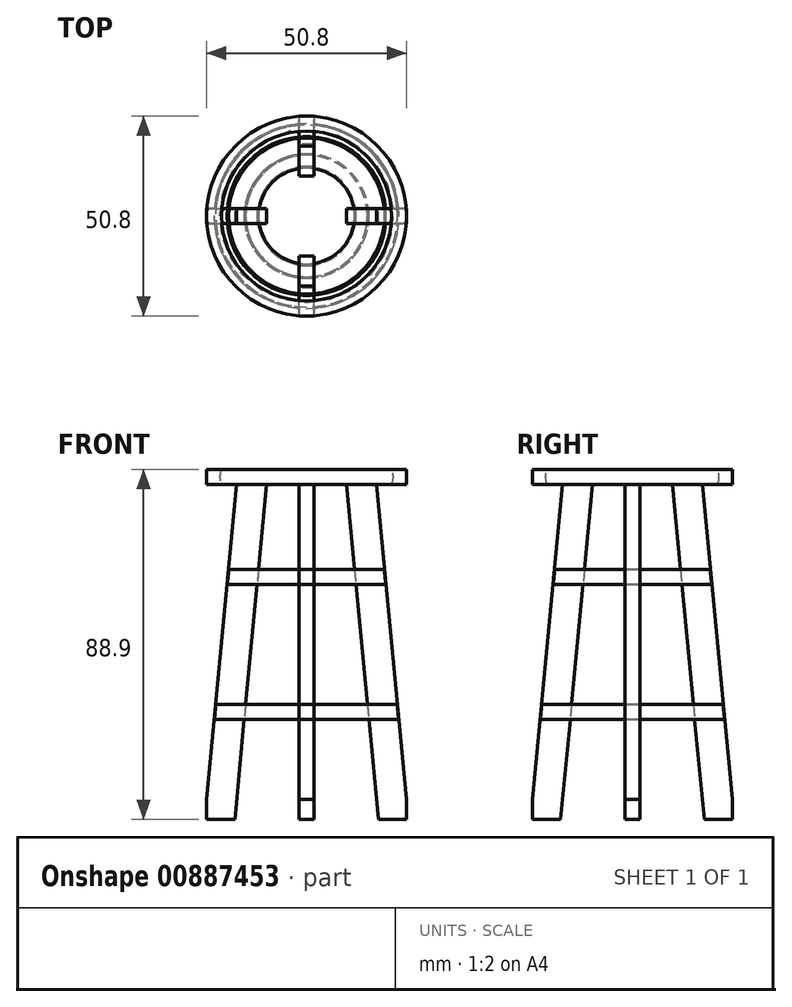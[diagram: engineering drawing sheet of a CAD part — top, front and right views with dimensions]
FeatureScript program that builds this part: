
annotation { "Feature Type Name" : "Feature", "Feature Type Description" : "" }
export const myFeature = defineFeature(function(context is Context, id is Id, definition is map)
    precondition{}
    {
        {
            var Q0;
            Q0=qCreatedBy(makeId("Front.planeOp"),FACE);
            var sketch = newSketch(context, id + "F0", { "sketchPlane" : qUnion([Q0])});
            skLineSegment(sketch, "E0.bottom", {"start": v(25.4, 44.45) * mm, "end": v(-25.4, 44.45) * mm});
            skLineSegment(sketch, "E0.top", {"start": v(25.4, -44.45) * mm, "end": v(-25.4, -44.45) * mm});
            skLineSegment(sketch, "E0.left", {"start": v(25.4, 44.45) * mm, "end": v(25.4, -44.45) * mm});
            skLineSegment(sketch, "E0.right", {"start": v(-25.4, 44.45) * mm, "end": v(-25.4, -44.45) * mm});
            skPoint(sketch, "E0.middle", {"position": v(0, 0) * mm});
            skLineSegment(sketch, "E1", {"start": v(-25.4, 40.64) * mm, "end": v(25.4, 40.64) * mm});
            skArc(sketch, "E2", {"start": v(-21.59, 40.64) * mm, "mid": v(-22.04, 42.55) * mm, "end": v(-21.59, 44.45) * mm});
            skArc(sketch, "E3", {"start": v(21.59, 44.45) * mm, "mid": v(22.04, 42.55) * mm, "end": v(21.6, 40.64) * mm});
            skPoint(sketch, "E4.end.orphan", {"position": v(21.59, 40.64) * mm});
            skPoint(sketch, "E5.start.orphan", {"position": v(21.59, 42.55) * mm});
            skPoint(sketch, "E6.start.orphan", {"position": v(-21.59, 44.45) * mm});
            skPoint(sketch, "E7.start.orphan", {"position": v(-21.59, 42.55) * mm});
            skLineSegment(sketch, "E8", {"start": v(-17.75, -39.37) * mm, "end": v(17.75, -39.37) * mm});
            skLineSegment(sketch, "E9", {"start": v(-25.4, -39.37) * mm, "end": v(-17.78, 40.64) * mm});
            skLineSegment(sketch, "E10", {"start": v(17.78, 40.64) * mm, "end": v(25.4, -39.37) * mm});
            skLineSegment(sketch, "E11", {"start": v(-18.23, -44.45) * mm, "end": v(-10.13, 40.64) * mm});
            skLineSegment(sketch, "E12", {"start": v(10.13, 40.64) * mm, "end": v(18.23, -44.45) * mm});
            skPoint(sketch, "E13.end.orphan", {"position": v(17.78, 0) * mm});
            skPoint(sketch, "E14.orphan", {"position": v(-25.4, 0) * mm});
            skPoint(sketch, "E15.orphan", {"position": v(25.4, 0) * mm});
            skLineSegment(sketch, "E16", {"start": v(-20.2, 15.24) * mm, "end": v(20.2, 15.24) * mm});
            skLineSegment(sketch, "E17", {"start": v(-23.46, -19.05) * mm, "end": v(23.46, -19.05) * mm});
            skLineSegment(sketch, "E18.0", {"start": v(-23.1, -15.24) * mm, "end": v(23.1, -15.24) * mm});
            skLineSegment(sketch, "E19.0", {"start": v(-19.84, 19.05) * mm, "end": v(19.84, 19.05) * mm});
            skLineSegment(sketch, "E20", {"start": v(0, 40.64) * mm, "end": v(0, 44.45) * mm});
            skLineSegment(sketch, "E21", {"start": v(0, 44.45) * mm, "end": v(0, 48.34) * mm});
            skLineSegment(sketch, "E22", {"start": v(0, 40.64) * mm, "end": v(0, 36.32) * mm});
            skLineSegment(sketch, "E23", {"start": v(0, 36.32) * mm, "end": v(0, 48.34) * mm});
            skPoint(sketch, "E24.endSnap0", {"position": v(0, 15.24) * mm});
            skPoint(sketch, "E24.end.orphan", {"position": v(0, 21.51) * mm});
            skLineSegment(sketch, "E25", {"start": v(0, 36.32) * mm, "end": v(0, -26.6) * mm});
            skSolve(sketch);
        }
        {
            var Q0;
            {var subQ5=sQuery(id+"F0.wireOp",EDGE,"E2");Q0=makeQuery(id+"F0.imprint","IMPRINT",FACE,{"disambiguationData":[TD([[makeQuery(id+"F0.imprint","IMPRINT",EDGE,{"derivedFrom":subQ5}),-1.0]])]});}
            var Q1;
            Q1=sQuery(id+"F0.wireOp",EDGE,"E20");
            revolve(context, id + "F1", {"surfaceOperationType" : NewSurfaceOperationType.NEW, "entities" : qUnion([Q0]), "axis" : qUnion([Q1]), "revolveType" : RevolveType.FULL});
        }
        {
            var Q0;
            {var subQ0=sQuery(id+"F0.wireOp",EDGE,"E9");var subQ1=sQuery(id+"F0.wireOp",EDGE,"E1");var subQ2=makeQuery(id+"F0.imprint","INTERSECT",VERTEX,{"derivedFrom":[subQ1,subQ0]});Q0=makeQuery(id+"F0.imprint","IMPRINT",FACE,{"disambiguationData":[TD([[makeQuery(id+"F0.imprint","IMPRINT",EDGE,{"disambiguationData":[TD([[subQ2,-1.0]])],"derivedFrom":subQ1}),-1.0]])]});}
            var Q1;
            {var subQ0=sQuery(id+"F0.wireOp",EDGE,"E16");var subQ1=sQuery(id+"F0.wireOp",EDGE,"E9");var subQ2=makeQuery(id+"F0.imprint","INTERSECT",VERTEX,{"derivedFrom":[subQ1,subQ0]});Q1=makeQuery(id+"F0.imprint","IMPRINT",FACE,{"disambiguationData":[TD([[makeQuery(id+"F0.imprint","IMPRINT",EDGE,{"disambiguationData":[TD([[subQ2,-1.0]])],"derivedFrom":subQ1}),-1.0]])]});}
            var Q2;
            {var subQ0=sQuery(id+"F0.wireOp",EDGE,"E16");var subQ1=sQuery(id+"F0.wireOp",EDGE,"E9");var subQ2=makeQuery(id+"F0.imprint","INTERSECT",VERTEX,{"derivedFrom":[subQ1,subQ0]});Q2=makeQuery(id+"F0.imprint","IMPRINT",FACE,{"disambiguationData":[TD([[makeQuery(id+"F0.imprint","IMPRINT",EDGE,{"disambiguationData":[TD([[subQ2,1.0]])],"derivedFrom":subQ1}),-1.0]])]});}
            var Q3;
            {var subQ0=sQuery(id+"F0.wireOp",EDGE,"E17");var subQ1=sQuery(id+"F0.wireOp",EDGE,"E9");var subQ2=makeQuery(id+"F0.imprint","INTERSECT",VERTEX,{"derivedFrom":[subQ1,subQ0]});Q3=makeQuery(id+"F0.imprint","IMPRINT",FACE,{"disambiguationData":[TD([[makeQuery(id+"F0.imprint","IMPRINT",EDGE,{"disambiguationData":[TD([[subQ2,-1.0]])],"derivedFrom":subQ1}),-1.0]])]});}
            var Q4;
            {var subQ2=sQuery(id+"F0.wireOp",EDGE,"E0.top");var subQ4=sQuery(id+"F0.wireOp",EDGE,"E0.right");var subQ5=makeQuery(id+"F0.imprint","INTERSECT",VERTEX,{"derivedFrom":[subQ2,subQ4]});Q4=makeQuery(id+"F0.imprint","IMPRINT",FACE,{"disambiguationData":[TD([[makeQuery(id+"F0.imprint","IMPRINT",EDGE,{"disambiguationData":[TD([[subQ5,1.0]])],"derivedFrom":subQ2}),-1.0]])]});}
            var Q5;
            {var subQ0=sQuery(id+"F0.wireOp",EDGE,"E17");var subQ1=sQuery(id+"F0.wireOp",EDGE,"E10");var subQ2=makeQuery(id+"F0.imprint","INTERSECT",VERTEX,{"derivedFrom":[subQ1,subQ0]});Q5=makeQuery(id+"F0.imprint","IMPRINT",FACE,{"disambiguationData":[TD([[makeQuery(id+"F0.imprint","IMPRINT",EDGE,{"disambiguationData":[TD([[subQ2,1.0]])],"derivedFrom":subQ1}),-1.0]])]});}
            var Q6;
            {var subQ1=sQuery(id+"F0.wireOp",EDGE,"E0.left");var subQ8=sQuery(id+"F0.wireOp",EDGE,"E0.top");var subQ9=makeQuery(id+"F0.imprint","INTERSECT",VERTEX,{"derivedFrom":[subQ8,subQ1]});Q6=makeQuery(id+"F0.imprint","IMPRINT",FACE,{"disambiguationData":[TD([[makeQuery(id+"F0.imprint","IMPRINT",EDGE,{"disambiguationData":[TD([[subQ9,-1.0]])],"derivedFrom":subQ8}),-1.0]])]});}
            var Q7;
            {var subQ0=sQuery(id+"F0.wireOp",EDGE,"E16");var subQ1=sQuery(id+"F0.wireOp",EDGE,"E10");var subQ2=makeQuery(id+"F0.imprint","INTERSECT",VERTEX,{"derivedFrom":[subQ1,subQ0]});Q7=makeQuery(id+"F0.imprint","IMPRINT",FACE,{"disambiguationData":[TD([[makeQuery(id+"F0.imprint","IMPRINT",EDGE,{"disambiguationData":[TD([[subQ2,-1.0]])],"derivedFrom":subQ1}),-1.0]])]});}
            var Q8;
            {var subQ0=sQuery(id+"F0.wireOp",EDGE,"E16");var subQ1=sQuery(id+"F0.wireOp",EDGE,"E10");var subQ2=makeQuery(id+"F0.imprint","INTERSECT",VERTEX,{"derivedFrom":[subQ1,subQ0]});Q8=makeQuery(id+"F0.imprint","IMPRINT",FACE,{"disambiguationData":[TD([[makeQuery(id+"F0.imprint","IMPRINT",EDGE,{"disambiguationData":[TD([[subQ2,1.0]])],"derivedFrom":subQ1}),-1.0]])]});}
            var Q9;
            {var subQ0=sQuery(id+"F0.wireOp",EDGE,"E10");var subQ1=sQuery(id+"F0.wireOp",EDGE,"E1");var subQ2=makeQuery(id+"F0.imprint","INTERSECT",VERTEX,{"derivedFrom":[subQ1,subQ0]});Q9=makeQuery(id+"F0.imprint","IMPRINT",FACE,{"disambiguationData":[TD([[makeQuery(id+"F0.imprint","IMPRINT",EDGE,{"disambiguationData":[TD([[subQ2,1.0]])],"derivedFrom":subQ1}),-1.0]])]});}
            extrude(context, id + "F2", {"entities" : qUnion([Q0, Q1, Q2, Q3, Q4, Q5, Q6, Q7, Q8, Q9]), "operationType" : NewBodyOperationType.ADD, "endBound" : BoundingType.SYMMETRIC, "depth" : 3.8 * mm, "offsetDistance" : 25.4 * mm});
        }
        {
            var Q0;
            Q0=qCreatedBy(makeId("Right.planeOp"),FACE);
            var sketch = newSketch(context, id + "F3", { "sketchPlane" : qUnion([Q0])});
            skLineSegment(sketch, "E26.bottom", {"start": v(25.4, 44.45) * mm, "end": v(-25.4, 44.45) * mm});
            skLineSegment(sketch, "E26.top", {"start": v(25.4, -44.45) * mm, "end": v(-25.4, -44.45) * mm});
            skLineSegment(sketch, "E26.left", {"start": v(25.4, 44.45) * mm, "end": v(25.4, -44.45) * mm});
            skLineSegment(sketch, "E26.right", {"start": v(-25.4, 44.45) * mm, "end": v(-25.4, -44.45) * mm});
            skPoint(sketch, "E26.middle", {"position": v(0, 0) * mm});
            skLineSegment(sketch, "E27", {"start": v(-25.4, 40.64) * mm, "end": v(25.4, 40.64) * mm});
            skArc(sketch, "E28", {"start": v(-25.1, 40.64) * mm, "mid": v(-25.56, 42.54) * mm, "end": v(-25.1, 44.45) * mm});
            skArc(sketch, "E29", {"start": v(21.6, 44.45) * mm, "mid": v(23.22, 42.54) * mm, "end": v(21.6, 40.64) * mm});
            skPoint(sketch, "E30.end.orphan", {"position": v(21.6, 40.64) * mm});
            skPoint(sketch, "E31.start.orphan", {"position": v(21.6, 42.54) * mm});
            skPoint(sketch, "E32.start.orphan", {"position": v(-25.1, 44.45) * mm});
            skPoint(sketch, "E33.start.orphan", {"position": v(-25.1, 42.54) * mm});
            skLineSegment(sketch, "E34", {"start": v(-17.75, -39.37) * mm, "end": v(17.75, -39.37) * mm});
            skLineSegment(sketch, "E35", {"start": v(-25.4, -39.37) * mm, "end": v(-17.78, 40.64) * mm});
            skLineSegment(sketch, "E36", {"start": v(17.78, 40.64) * mm, "end": v(25.4, -39.37) * mm});
            skLineSegment(sketch, "E37", {"start": v(-18.23, -44.45) * mm, "end": v(-10.13, 40.64) * mm});
            skLineSegment(sketch, "E38", {"start": v(10.13, 40.64) * mm, "end": v(18.23, -44.45) * mm});
            skPoint(sketch, "E39.end.orphan", {"position": v(17.78, 0) * mm});
            skPoint(sketch, "E40.orphan", {"position": v(-25.4, 0) * mm});
            skPoint(sketch, "E41.orphan", {"position": v(25.4, 0) * mm});
            skLineSegment(sketch, "E42", {"start": v(-20.2, 15.24) * mm, "end": v(20.2, 15.24) * mm});
            skLineSegment(sketch, "E43", {"start": v(-23.46, -19.05) * mm, "end": v(23.46, -19.05) * mm});
            skLineSegment(sketch, "E44.0", {"start": v(-23.1, -15.24) * mm, "end": v(23.1, -15.24) * mm});
            skLineSegment(sketch, "E45.0", {"start": v(-19.84, 19.05) * mm, "end": v(19.84, 19.05) * mm});
            skLineSegment(sketch, "E46", {"start": v(0, 40.64) * mm, "end": v(0, 44.45) * mm});
            skLineSegment(sketch, "E47", {"start": v(0, 44.45) * mm, "end": v(0, 47.53) * mm});
            skLineSegment(sketch, "E48", {"start": v(0, 40.64) * mm, "end": v(0, 35.5) * mm});
            skLineSegment(sketch, "E49", {"start": v(0, 35.5) * mm, "end": v(0, 47.53) * mm});
            skPoint(sketch, "E50.endSnap0", {"position": v(0, 15.24) * mm});
            skPoint(sketch, "E50.end.orphan", {"position": v(0, 21.51) * mm});
            skLineSegment(sketch, "E51", {"start": v(0, 35.5) * mm, "end": v(0, -27.43) * mm});
            skLineSegment(sketch, "E52", {"start": v(21.6, 44.45) * mm, "end": v(21.6, 40.64) * mm});
            skLineSegment(sketch, "E53", {"start": v(17.78, 40.64) * mm, "end": v(17.78, 44.45) * mm});
            skSolve(sketch);
        }
        {
            var Q0;
            {var subQ0=sQuery(id+"F3.wireOp",EDGE,"E35");var subQ1=sQuery(id+"F3.wireOp",EDGE,"E27");var subQ2=makeQuery(id+"F3.imprint","INTERSECT",VERTEX,{"derivedFrom":[subQ1,subQ0]});Q0=makeQuery(id+"F3.imprint","IMPRINT",FACE,{"disambiguationData":[TD([[makeQuery(id+"F3.imprint","IMPRINT",EDGE,{"disambiguationData":[TD([[subQ2,-1.0]])],"derivedFrom":subQ1}),-1.0]])]});}
            var Q1;
            {var subQ0=sQuery(id+"F3.wireOp",EDGE,"E42");var subQ1=sQuery(id+"F3.wireOp",EDGE,"E35");var subQ2=makeQuery(id+"F3.imprint","INTERSECT",VERTEX,{"derivedFrom":[subQ1,subQ0]});Q1=makeQuery(id+"F3.imprint","IMPRINT",FACE,{"disambiguationData":[TD([[makeQuery(id+"F3.imprint","IMPRINT",EDGE,{"disambiguationData":[TD([[subQ2,-1.0]])],"derivedFrom":subQ1}),-1.0]])]});}
            var Q2;
            {var subQ0=sQuery(id+"F3.wireOp",EDGE,"E36");var subQ1=sQuery(id+"F3.wireOp",EDGE,"E27");var subQ2=makeQuery(id+"F3.imprint","INTERSECT",VERTEX,{"derivedFrom":[subQ1,subQ0]});Q2=makeQuery(id+"F3.imprint","IMPRINT",FACE,{"disambiguationData":[TD([[makeQuery(id+"F3.imprint","IMPRINT",EDGE,{"disambiguationData":[TD([[subQ2,1.0]])],"derivedFrom":subQ1}),-1.0]])]});}
            var Q3;
            {var subQ0=sQuery(id+"F3.wireOp",EDGE,"E42");var subQ1=sQuery(id+"F3.wireOp",EDGE,"E36");var subQ2=makeQuery(id+"F3.imprint","INTERSECT",VERTEX,{"derivedFrom":[subQ1,subQ0]});Q3=makeQuery(id+"F3.imprint","IMPRINT",FACE,{"disambiguationData":[TD([[makeQuery(id+"F3.imprint","IMPRINT",EDGE,{"disambiguationData":[TD([[subQ2,1.0]])],"derivedFrom":subQ1}),-1.0]])]});}
            var Q4;
            {var subQ0=sQuery(id+"F3.wireOp",EDGE,"E42");var subQ1=sQuery(id+"F3.wireOp",EDGE,"E36");var subQ2=makeQuery(id+"F3.imprint","INTERSECT",VERTEX,{"derivedFrom":[subQ1,subQ0]});Q4=makeQuery(id+"F3.imprint","IMPRINT",FACE,{"disambiguationData":[TD([[makeQuery(id+"F3.imprint","IMPRINT",EDGE,{"disambiguationData":[TD([[subQ2,-1.0]])],"derivedFrom":subQ1}),-1.0]])]});}
            var Q5;
            {var subQ0=sQuery(id+"F3.wireOp",EDGE,"E42");var subQ1=sQuery(id+"F3.wireOp",EDGE,"E35");var subQ2=makeQuery(id+"F3.imprint","INTERSECT",VERTEX,{"derivedFrom":[subQ1,subQ0]});Q5=makeQuery(id+"F3.imprint","IMPRINT",FACE,{"disambiguationData":[TD([[makeQuery(id+"F3.imprint","IMPRINT",EDGE,{"disambiguationData":[TD([[subQ2,1.0]])],"derivedFrom":subQ1}),-1.0]])]});}
            var Q6;
            {var subQ0=sQuery(id+"F3.wireOp",EDGE,"E43");var subQ1=sQuery(id+"F3.wireOp",EDGE,"E35");var subQ2=makeQuery(id+"F3.imprint","INTERSECT",VERTEX,{"derivedFrom":[subQ1,subQ0]});Q6=makeQuery(id+"F3.imprint","IMPRINT",FACE,{"disambiguationData":[TD([[makeQuery(id+"F3.imprint","IMPRINT",EDGE,{"disambiguationData":[TD([[subQ2,-1.0]])],"derivedFrom":subQ1}),-1.0]])]});}
            var Q7;
            {var subQ2=sQuery(id+"F3.wireOp",EDGE,"E26.top");var subQ5=sQuery(id+"F3.wireOp",EDGE,"E26.right");var subQ9=makeQuery(id+"F3.imprint","INTERSECT",VERTEX,{"derivedFrom":[subQ2,subQ5]});Q7=makeQuery(id+"F3.imprint","IMPRINT",FACE,{"disambiguationData":[TD([[makeQuery(id+"F3.imprint","IMPRINT",EDGE,{"disambiguationData":[TD([[subQ9,1.0]])],"derivedFrom":subQ2}),-1.0]])]});}
            var Q8;
            {var subQ5=sQuery(id+"F3.wireOp",EDGE,"E26.left");var subQ8=sQuery(id+"F3.wireOp",EDGE,"E26.top");var subQ9=makeQuery(id+"F3.imprint","INTERSECT",VERTEX,{"derivedFrom":[subQ8,subQ5]});Q8=makeQuery(id+"F3.imprint","IMPRINT",FACE,{"disambiguationData":[TD([[makeQuery(id+"F3.imprint","IMPRINT",EDGE,{"disambiguationData":[TD([[subQ9,-1.0]])],"derivedFrom":subQ8}),-1.0]])]});}
            var Q9;
            {var subQ0=sQuery(id+"F3.wireOp",EDGE,"E43");var subQ1=sQuery(id+"F3.wireOp",EDGE,"E36");var subQ2=makeQuery(id+"F3.imprint","INTERSECT",VERTEX,{"derivedFrom":[subQ1,subQ0]});Q9=makeQuery(id+"F3.imprint","IMPRINT",FACE,{"disambiguationData":[TD([[makeQuery(id+"F3.imprint","IMPRINT",EDGE,{"disambiguationData":[TD([[subQ2,1.0]])],"derivedFrom":subQ1}),-1.0]])]});}
            extrude(context, id + "F4", {"entities" : qUnion([Q0, Q1, Q2, Q3, Q4, Q5, Q6, Q7, Q8, Q9]), "operationType" : NewBodyOperationType.ADD, "endBound" : BoundingType.SYMMETRIC, "depth" : 3.8 * mm, "offsetDistance" : 25.4 * mm});
        }
        {
            var Q0;
            {var subQ0=sQuery(id+"F3.wireOp",EDGE,"E42");var subQ1=sQuery(id+"F3.wireOp",EDGE,"E36");var subQ2=makeQuery(id+"F3.imprint","INTERSECT",VERTEX,{"derivedFrom":[subQ1,subQ0]});Q0=makeQuery(id+"F3.imprint","IMPRINT",FACE,{"disambiguationData":[TD([[makeQuery(id+"F3.imprint","IMPRINT",EDGE,{"disambiguationData":[TD([[subQ2,1.0]])],"derivedFrom":subQ1}),-1.0]])]});}
            var Q1;
            Q1=sQuery(id+"F3.wireOp",EDGE,"E51");
            revolve(context, id + "F5", {"surfaceOperationType" : NewSurfaceOperationType.NEW, "entities" : qUnion([Q0]), "axis" : qUnion([Q1]), "revolveType" : RevolveType.FULL});
        }
        {
            var Q0;
            {var subQ0=sQuery(id+"F3.wireOp",EDGE,"E43");var subQ1=sQuery(id+"F3.wireOp",EDGE,"E36");var subQ2=makeQuery(id+"F3.imprint","INTERSECT",VERTEX,{"derivedFrom":[subQ1,subQ0]});Q0=makeQuery(id+"F3.imprint","IMPRINT",FACE,{"disambiguationData":[TD([[makeQuery(id+"F3.imprint","IMPRINT",EDGE,{"disambiguationData":[TD([[subQ2,1.0]])],"derivedFrom":subQ1}),-1.0]])]});}
            var Q1;
            Q1=sQuery(id+"F3.wireOp",EDGE,"E51");
            revolve(context, id + "F6", {"surfaceOperationType" : NewSurfaceOperationType.NEW, "entities" : qUnion([Q0]), "axis" : qUnion([Q1]), "revolveType" : RevolveType.FULL});
        }
    });
